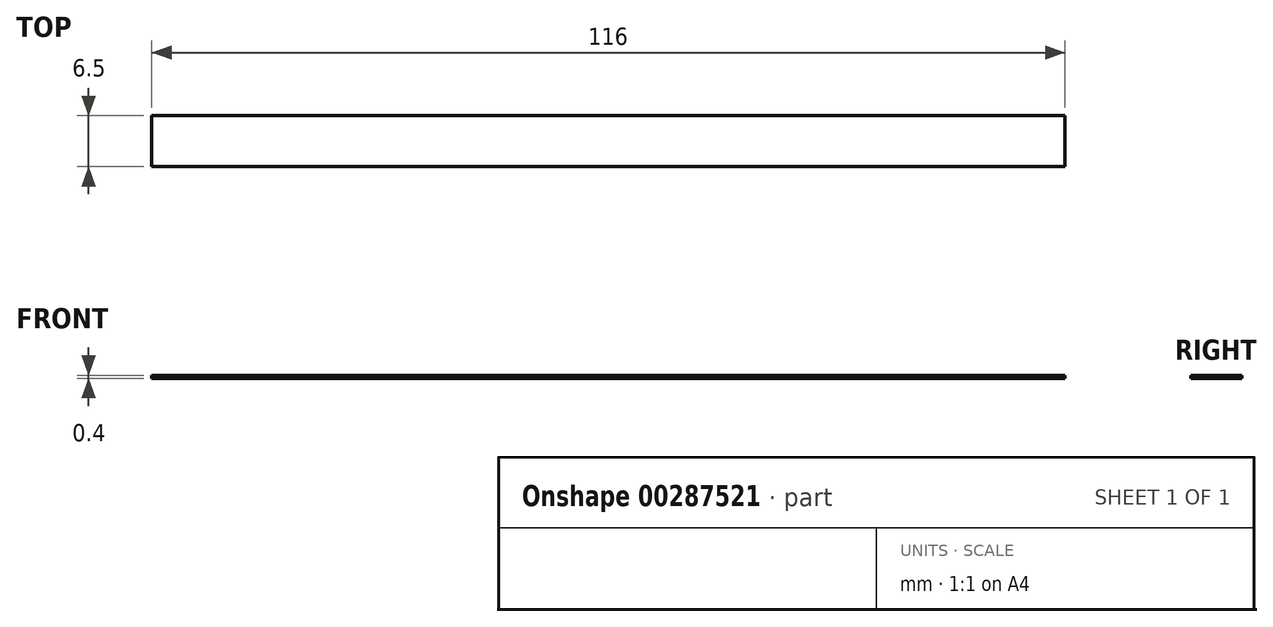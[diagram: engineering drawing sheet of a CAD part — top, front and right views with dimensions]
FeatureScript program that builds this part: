
annotation { "Feature Type Name" : "Feature", "Feature Type Description" : "" }
export const myFeature = defineFeature(function(context is Context, id is Id, definition is map)
    precondition{}
    {
        {
            var Q0;
            Q0=qCreatedBy(makeId("Top.planeOp"),FACE);
            var sketch = newSketch(context, id + "F0", { "sketchPlane" : qUnion([Q0])});
            skLineSegment(sketch, "E0.bottom", {"start": v(58, -3.25) * mm, "end": v(-58, -3.25) * mm});
            skLineSegment(sketch, "E0.top", {"start": v(58, 3.25) * mm, "end": v(-58, 3.25) * mm});
            skLineSegment(sketch, "E0.left", {"start": v(58, -3.25) * mm, "end": v(58, 3.25) * mm});
            skLineSegment(sketch, "E0.right", {"start": v(-58, -3.25) * mm, "end": v(-58, 3.25) * mm});
            skPoint(sketch, "E0.middle", {"position": v(0, 0) * mm});
            skSolve(sketch);
        }
        {
            var Q0;
            Q0 = qSketchRegion(id + "F0", true);
            extrude(context, id + "F1", {"entities" : qUnion([Q0]), "endBound" : BoundingType.SYMMETRIC, "depth" : .4 * mm});
        }
    });
